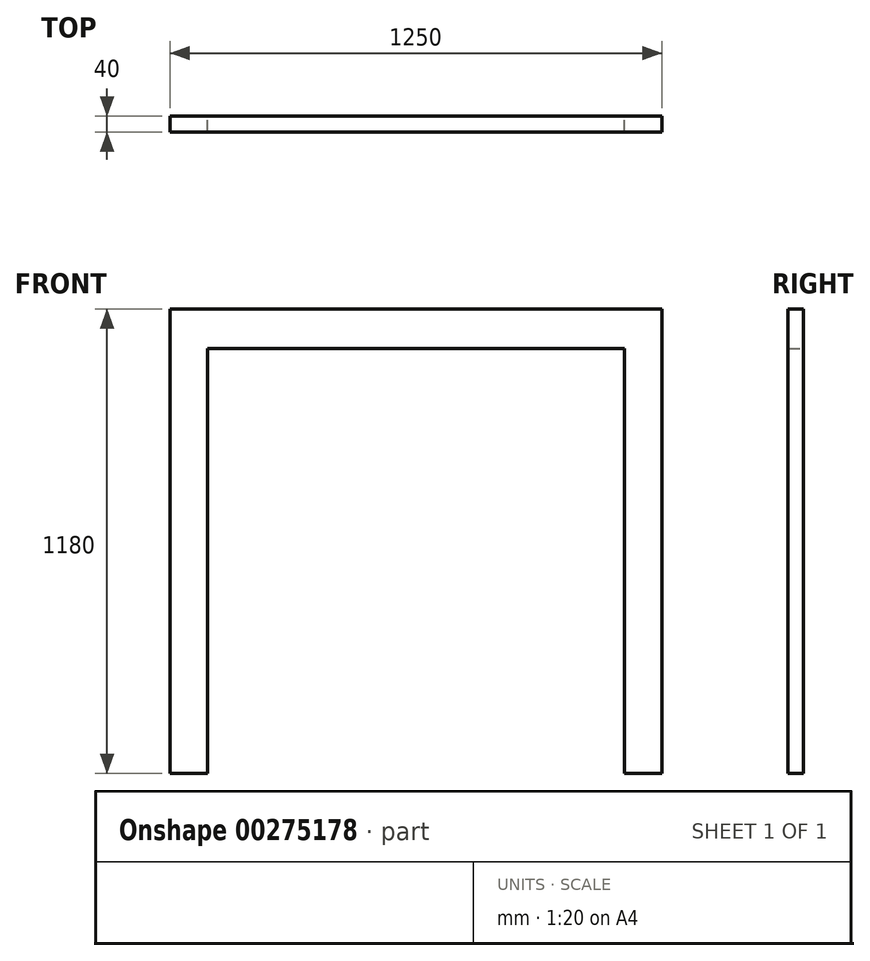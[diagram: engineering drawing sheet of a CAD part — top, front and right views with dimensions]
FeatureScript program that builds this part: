
annotation { "Feature Type Name" : "Feature", "Feature Type Description" : "" }
export const myFeature = defineFeature(function(context is Context, id is Id, definition is map)
    precondition{}
    {
        {
            var Q0;
            Q0=qCreatedBy(makeId("Front.planeOp"),FACE);
            var sketch = newSketch(context, id + "F0", { "sketchPlane" : qUnion([Q0])});
            skLineSegment(sketch, "E0", {"start": v(0, 0) * mm, "end": v(-530, 0) * mm, "construction": true});
            skLineSegment(sketch, "E1", {"start": v(-530, 0) * mm, "end": v(-530, 1080) * mm});
            skLineSegment(sketch, "E2", {"start": v(-530, 1080) * mm, "end": v(530, 1080) * mm});
            skLineSegment(sketch, "E3", {"start": v(530, 1080) * mm, "end": v(530, 0) * mm});
            skLineSegment(sketch, "E4", {"start": v(530, 0) * mm, "end": v(0, 0) * mm, "construction": true});
            skLineSegment(sketch, "E5", {"start": v(-530, 0) * mm, "end": v(-625, 0) * mm});
            skLineSegment(sketch, "E6", {"start": v(-625, 0) * mm, "end": v(-625, 1180) * mm});
            skLineSegment(sketch, "E7", {"start": v(-625, 1180) * mm, "end": v(625, 1180) * mm});
            skLineSegment(sketch, "E8", {"start": v(625, 1180) * mm, "end": v(625, 0) * mm});
            skLineSegment(sketch, "E9", {"start": v(625, 0) * mm, "end": v(530, 0) * mm});
            skSolve(sketch);
        }
        {
            var Q0;
            Q0 = qSketchRegion(id + "F0", true);
            extrude(context, id + "F1", {"entities" : qUnion([Q0]), "depth" : 40 * mm, "offsetDistance" : 25 * mm});
        }
    });
